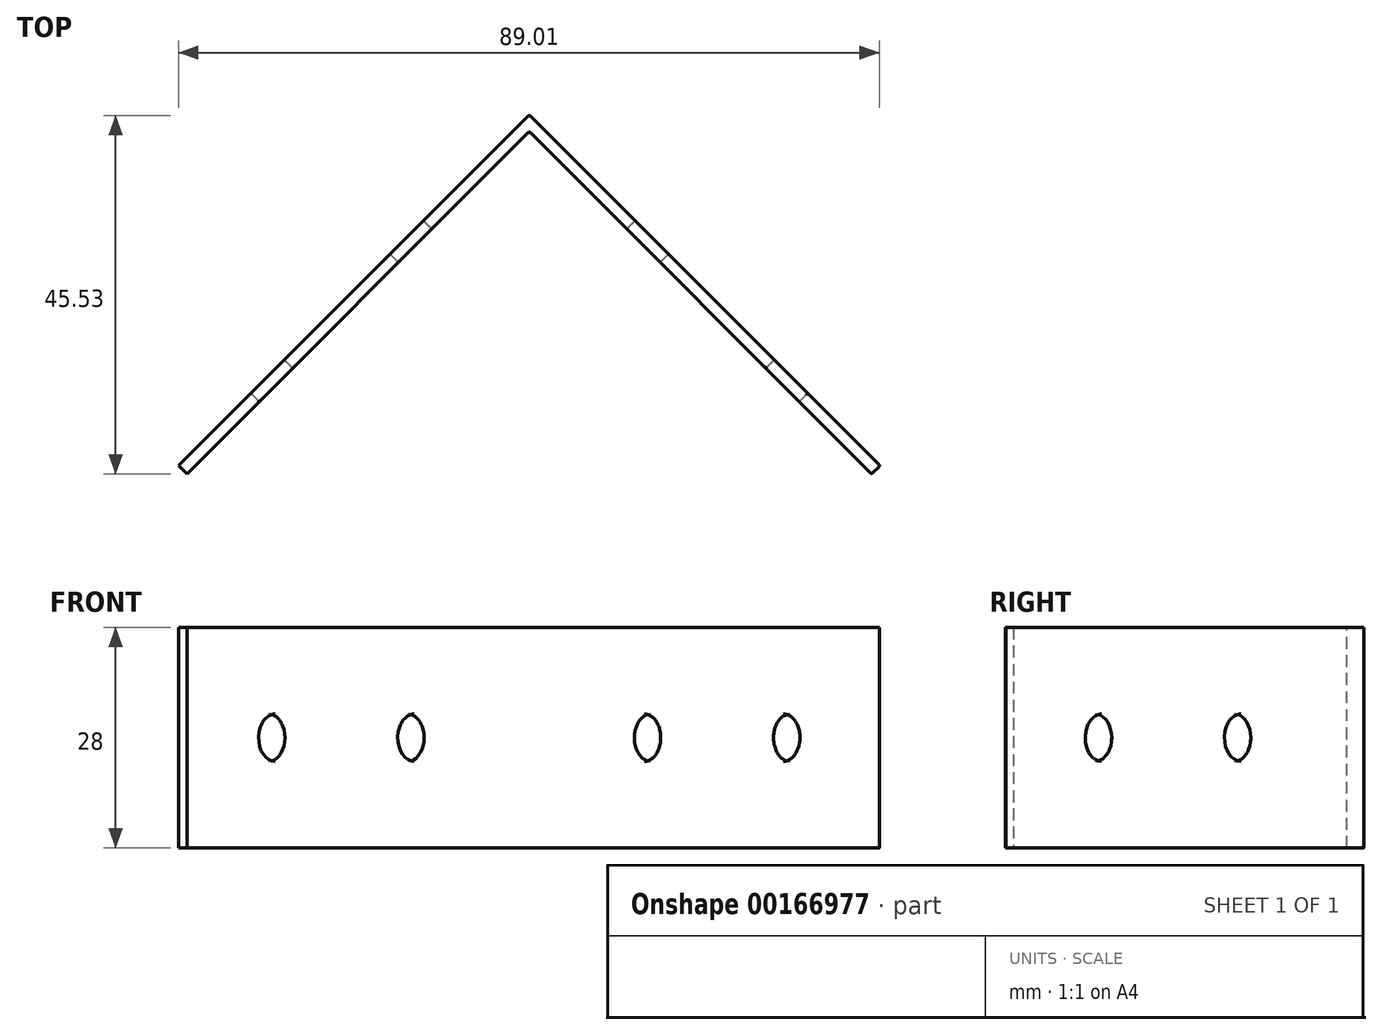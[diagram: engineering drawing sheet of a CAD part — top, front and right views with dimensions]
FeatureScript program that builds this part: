
annotation { "Feature Type Name" : "Feature", "Feature Type Description" : "" }
export const myFeature = defineFeature(function(context is Context, id is Id, definition is map)
    precondition{}
    {
        {
            var Q0;
            Q0=qCreatedBy(makeId("Top.planeOp"),FACE);
            var sketch = newSketch(context, id + "F0", { "sketchPlane" : qUnion([Q0])});
            skLineSegment(sketch, "E0", {"start": v(0, 0) * mm, "end": v(44.55, -44.55) * mm});
            skLineSegment(sketch, "E1", {"start": v(44.55, -44.55) * mm, "end": v(43.49, -45.6) * mm});
            skLineSegment(sketch, "E2", {"start": v(43.49, -45.6) * mm, "end": v(0, -2.12) * mm});
            skLineSegment(sketch, "E3", {"start": v(0, -2.12) * mm, "end": v(0, 0) * mm});
            skSolve(sketch);
        }
        {
            var Q0;
            Q0 = qSketchRegion(id + "F0", true);
            extrude(context, id + "F1", {"entities" : qUnion([Q0]), "depth" : 28 * mm});
        }
        {
            var Q0;
            Q0=makeQuery(id+"F1.opExtrude","SWEPT_FACE",FACE,{"disambiguationData":[OSD([sQuery(id+"F0.wireOp",EDGE,"E0")])]});
            var sketch = newSketch(context, id + "F2", { "sketchPlane" : qUnion([Q0])});
            skLineSegment(sketch, "E4", {"start": v(-63, 14) * mm, "end": v(0, 14) * mm, "construction": true});
            skCircle(sketch, "E5", {"center": v(-47, 14) * mm, "radius": 3 * mm});
            skCircle(sketch, "E6", {"center": v(-22, 14) * mm, "radius": 3 * mm});
            skSolve(sketch);
        }
        {
            var Q0;
            Q0=makeQuery(id+"F2.imprint","IMPRINT",FACE,{"disambiguationData":[TD([[makeQuery(id+"F2.imprint","IMPRINT",EDGE,{"derivedFrom":sQuery(id+"F2.wireOp",EDGE,"E6")}),1.0]])]});
            var Q1;
            Q1=makeQuery(id+"F2.imprint","IMPRINT",FACE,{"disambiguationData":[TD([[makeQuery(id+"F2.imprint","IMPRINT",EDGE,{"derivedFrom":sQuery(id+"F2.wireOp",EDGE,"E5")}),1.0]])]});
            extrude(context, id + "F3", {"entities" : qUnion([Q0, Q1]), "operationType" : NewBodyOperationType.REMOVE, "oppositeDirection" : true, "depth" : 2 * mm});
        }
        {
            var Q0;
            Q0=makeQuery(id+"F1.opExtrude","SWEPT_BODY",BODY,{"disambiguationData":[OSD([sQuery(id+"F0.wireOp",EDGE,"E0"),sQuery(id+"F0.wireOp",EDGE,"E1"),sQuery(id+"F0.wireOp",EDGE,"E2"),sQuery(id+"F0.wireOp",EDGE,"E3")])]});
            var Q1;
            Q1=qCreatedBy(makeId("Right.planeOp"),FACE);
            mirror(context, id + "F4", {"operationType" : NewBodyOperationType.ADD, "entities" : qUnion([Q0]), "mirrorPlane" : qUnion([Q1])});
        }
        {
            var Q0;
            Q0=makeQuery(id+"F1.opExtrude","SWEPT_EDGE",EDGE,{"disambiguationData":[OSD([sQuery(id+"F0.wireOp",EDGE,"E0"),sQuery(id+"F0.wireOp",EDGE,"E1")])]});
            var Q1;
            Q1=makeQuery(id+"F1.opExtrude","SWEPT_EDGE",EDGE,{"disambiguationData":[OSD([sQuery(id+"F0.wireOp",EDGE,"E1"),sQuery(id+"F0.wireOp",EDGE,"E2")])]});
            var Q2;
            {var subQ0=makeQuery(id+"F1.opExtrude","SWEPT_EDGE",EDGE,{"disambiguationData":[OSD([sQuery(id+"F0.wireOp",EDGE,"E0"),sQuery(id+"F0.wireOp",EDGE,"E3")])]});Q2=makeQuery(id+"F4.boolean.opBoolean","MERGE",EDGE,{"derivedFrom":[subQ0,makeQuery(id+"F4.opPattern","COPY",EDGE,{"derivedFrom":subQ0,"instanceName":"1"})]});}
            var Q3;
            {var subQ0=makeQuery(id+"F1.opExtrude","SWEPT_EDGE",EDGE,{"disambiguationData":[OSD([sQuery(id+"F0.wireOp",EDGE,"E2"),sQuery(id+"F0.wireOp",EDGE,"E3")])]});Q3=makeQuery(id+"F4.boolean.opBoolean","MERGE",EDGE,{"derivedFrom":[subQ0,makeQuery(id+"F4.opPattern","COPY",EDGE,{"derivedFrom":subQ0,"instanceName":"1"})]});}
            var Q4;
            Q4=makeQuery(id+"F4.opPattern","COPY",FACE,{"derivedFrom":makeQuery(id+"F3.boolean.opBoolean","COPY",FACE,{"derivedFrom":makeQuery(id+"F3.opExtrude","SWEPT_FACE",FACE,{"disambiguationData":[OSD([sQuery(id+"F2.wireOp",EDGE,"E6")])]})}),"instanceName":"1"});
            var Q5;
            Q5=makeQuery(id+"F4.opPattern","COPY",FACE,{"derivedFrom":makeQuery(id+"F3.boolean.opBoolean","COPY",FACE,{"derivedFrom":makeQuery(id+"F3.opExtrude","SWEPT_FACE",FACE,{"disambiguationData":[OSD([sQuery(id+"F2.wireOp",EDGE,"E5")])]})}),"instanceName":"1"});
            var Q6;
            Q6=makeQuery(id+"F3.boolean.opBoolean","COPY",FACE,{"derivedFrom":makeQuery(id+"F3.opExtrude","SWEPT_FACE",FACE,{"disambiguationData":[OSD([sQuery(id+"F2.wireOp",EDGE,"E6")])]})});
            var Q7;
            Q7=makeQuery(id+"F3.boolean.opBoolean","COPY",FACE,{"derivedFrom":makeQuery(id+"F3.opExtrude","SWEPT_FACE",FACE,{"disambiguationData":[OSD([sQuery(id+"F2.wireOp",EDGE,"E5")])]})});
            fillet(context, id + "F5", {"entities" : qUnion([Q0, Q1, Q2, Q3, Q4, Q5, Q6, Q7]), "radius" : 0.2 * mm, "tangentPropagation" : true, "allowEdgeOverflow" : false});
        }
    });
